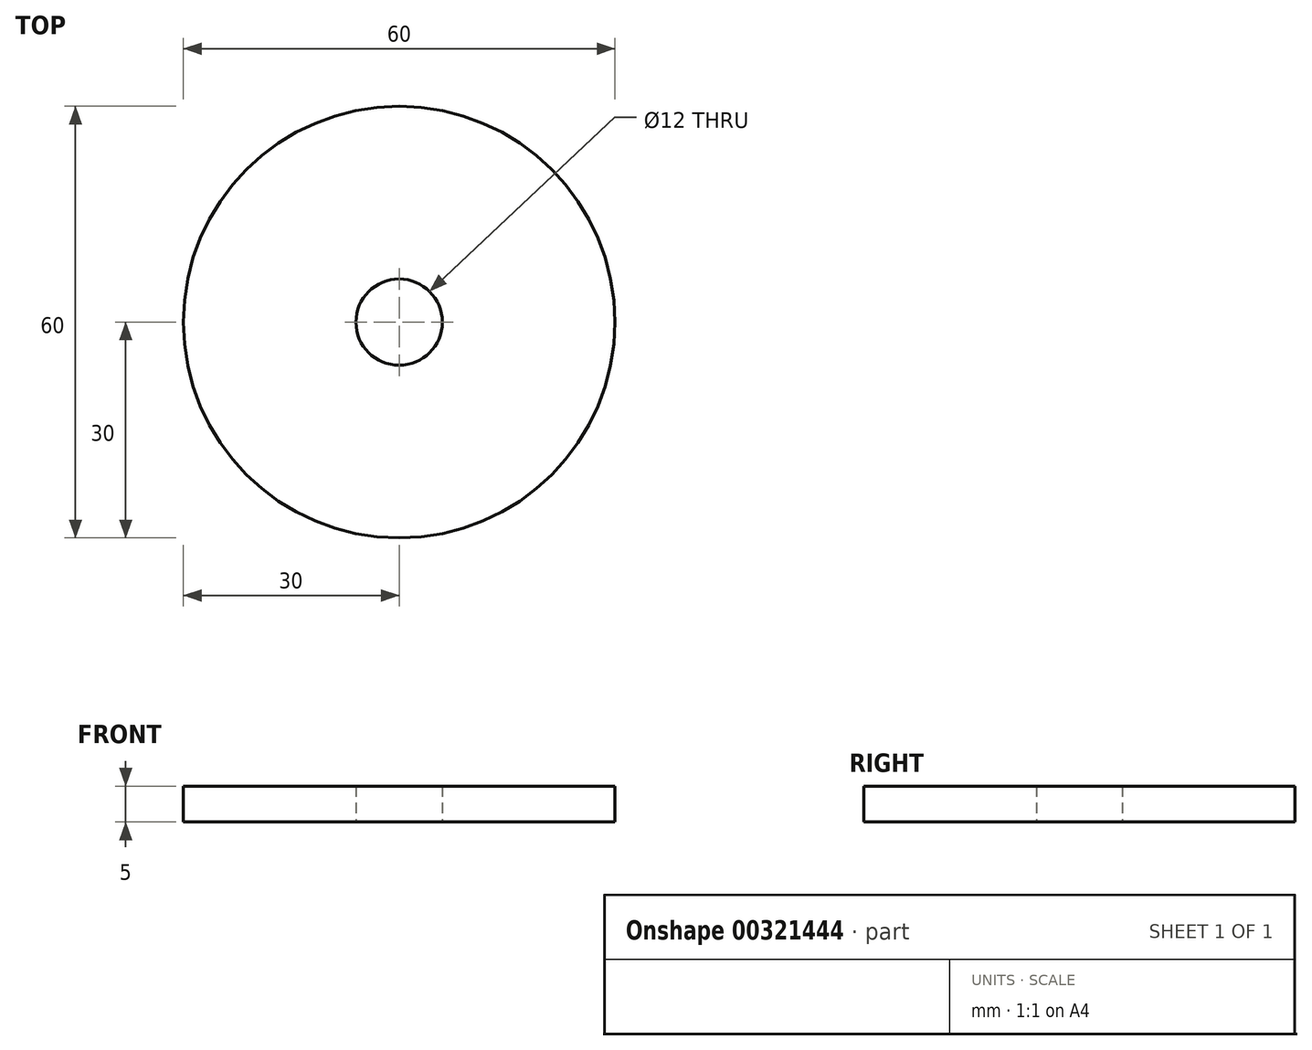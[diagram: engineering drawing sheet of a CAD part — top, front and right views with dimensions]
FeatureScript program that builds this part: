
annotation { "Feature Type Name" : "Feature", "Feature Type Description" : "" }
export const myFeature = defineFeature(function(context is Context, id is Id, definition is map)
    precondition{}
    {
        {
            var Q0;
            Q0=qCreatedBy(makeId("Top.planeOp"),FACE);
            var sketch = newSketch(context, id + "F0", { "sketchPlane" : qUnion([Q0])});
            skCircle(sketch, "E0", {"center": v(0, 0) * mm, "radius": 30 * mm});
            skCircle(sketch, "E1", {"center": v(0, 0) * mm, "radius": 6 * mm});
            skSolve(sketch);
        }
        {
            var Q0;
            Q0 = qSketchRegion(id + "F0", true);
            extrude(context, id + "F1", {"entities" : qUnion([Q0]), "depth" : 5 * mm});
        }
    });
